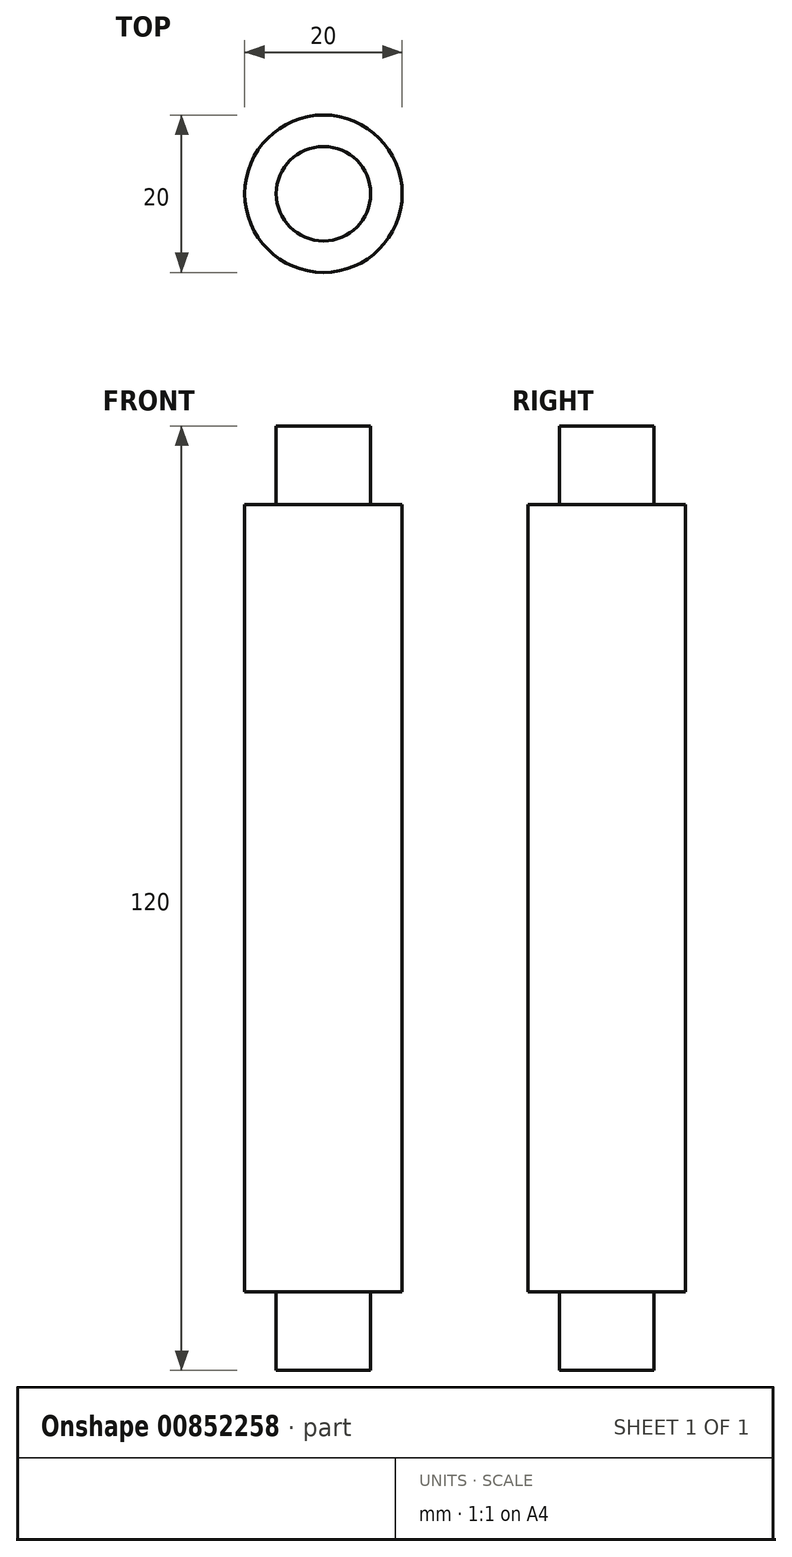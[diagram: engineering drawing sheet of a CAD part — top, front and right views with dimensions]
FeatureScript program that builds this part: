
annotation { "Feature Type Name" : "Feature", "Feature Type Description" : "" }
export const myFeature = defineFeature(function(context is Context, id is Id, definition is map)
    precondition{}
    {
        {
            var Q0;
            Q0=qCreatedBy(makeId("Front.planeOp"),FACE);
            var sketch = newSketch(context, id + "F0", { "sketchPlane" : qUnion([Q0])});
            skLineSegment(sketch, "E0", {"start": v(0, 0) * mm, "end": v(-6, 0) * mm});
            skLineSegment(sketch, "E1", {"start": v(-6, 0) * mm, "end": v(-6, 10) * mm});
            skLineSegment(sketch, "E2", {"start": v(-6, 10) * mm, "end": v(-10, 10) * mm});
            skLineSegment(sketch, "E3", {"start": v(-10, 10) * mm, "end": v(-10, 110) * mm});
            skLineSegment(sketch, "E4", {"start": v(-10, 110) * mm, "end": v(-6, 110) * mm});
            skLineSegment(sketch, "E5", {"start": v(-6, 110) * mm, "end": v(-6, 120) * mm});
            skLineSegment(sketch, "E6", {"start": v(-6, 120) * mm, "end": v(0, 120) * mm});
            skLineSegment(sketch, "E7", {"start": v(0, 120) * mm, "end": v(0, 0) * mm});
            skSolve(sketch);
        }
        {
            var Q0;
            Q0 = qSketchRegion(id + "F0", true);
            var Q1;
            Q1=sQuery(id+"F0.wireOp",EDGE,"E7");
            revolve(context, id + "F1", {"surfaceOperationType" : NewSurfaceOperationType.NEW, "entities" : qUnion([Q0]), "axis" : qUnion([Q1]), "revolveType" : RevolveType.FULL});
        }
    });
